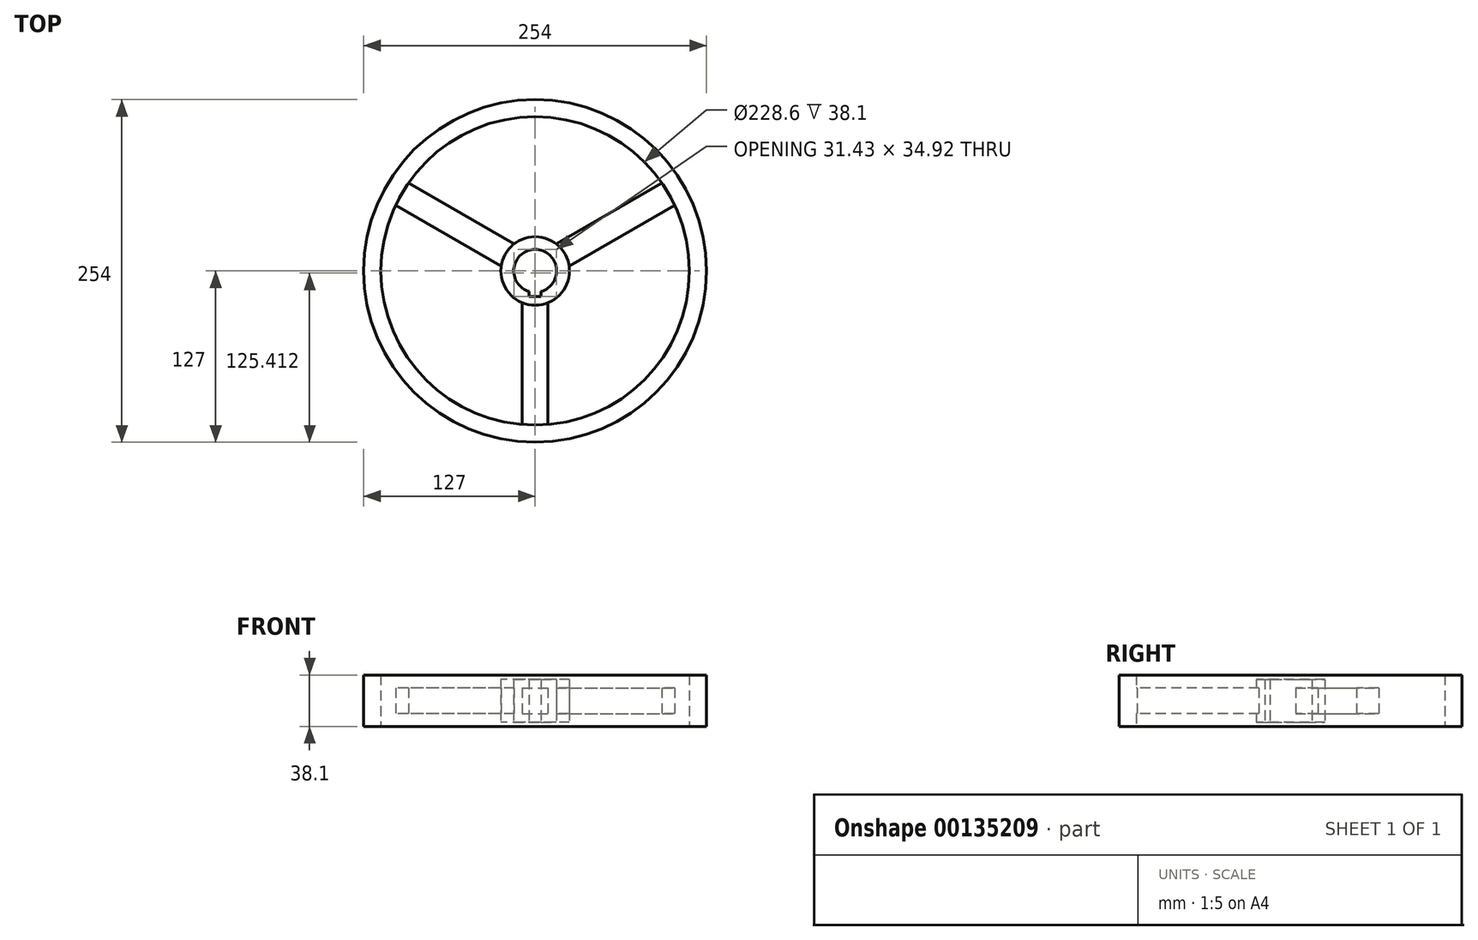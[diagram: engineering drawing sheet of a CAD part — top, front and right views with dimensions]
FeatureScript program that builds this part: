
annotation { "Feature Type Name" : "Feature", "Feature Type Description" : "" }
export const myFeature = defineFeature(function(context is Context, id is Id, definition is map)
    precondition{}
    {
        {
            var Q0;
            Q0=qCreatedBy(makeId("Top.planeOp"),FACE);
            var sketch = newSketch(context, id + "F0", { "sketchPlane" : qUnion([Q0])});
            skLineSegment(sketch, "E0", {"start": v(-303.2, 175.05) * mm, "end": v(0, 0) * mm, "construction": true});
            skLineSegment(sketch, "E1", {"start": v(0, 0) * mm, "end": v(0, -304.21) * mm, "construction": true});
            skArc(sketch, "E2", {"start": v(-98.99, 57.15) * mm, "mid": v(-98.99, -57.15) * mm, "end": v(0, -114.3) * mm});
            skArc(sketch, "E3", {"start": v(-109.99, 63.5) * mm, "mid": v(-109.99, -63.5) * mm, "end": v(0, -127) * mm});
            skArc(sketch, "E4", {"start": v(-13.75, 7.94) * mm, "mid": v(-14.73, -5.91) * mm, "end": v(-4.45, -15.24) * mm});
            skArc(sketch, "E5", {"start": v(-22, 12.7) * mm, "mid": v(-22, -12.7) * mm, "end": v(0, -25.4) * mm});
            skLineSegment(sketch, "E6", {"start": v(-9.53, -23.55) * mm, "end": v(-9.53, -113.9) * mm});
            skLineSegment(sketch, "E7", {"start": v(-25.15, 3.52) * mm, "end": v(-103.4, 48.7) * mm});
            skArc(sketch, "E8", {"start": v(0, -127) * mm, "mid": v(109.99, 63.5) * mm, "end": v(-109.99, 63.5) * mm});
            skArc(sketch, "E9", {"start": v(0, -114.3) * mm, "mid": v(98.99, 57.15) * mm, "end": v(-98.99, 57.15) * mm});
            skArc(sketch, "E10", {"start": v(0, -25.4) * mm, "mid": v(22, 12.7) * mm, "end": v(-22, 12.7) * mm});
            skArc(sketch, "E11", {"start": v(4.44, -15.24) * mm, "mid": v(12.49, 9.8) * mm, "end": v(-13.75, 7.94) * mm});
            skLineSegment(sketch, "E12", {"start": v(9.52, -23.55) * mm, "end": v(9.52, -113.9) * mm});
            skLineSegment(sketch, "E13", {"start": v(-15.63, 20.02) * mm, "end": v(-93.88, 65.2) * mm});
            skLineSegment(sketch, "E14", {"start": v(15.63, 20.02) * mm, "end": v(93.88, 65.2) * mm});
            skLineSegment(sketch, "E15", {"start": v(25.15, 3.52) * mm, "end": v(103.4, 48.7) * mm});
            skLineSegment(sketch, "E16", {"start": v(0, 0) * mm, "end": v(160.47, 92.65) * mm, "construction": true});
            skLineSegment(sketch, "E17", {"start": v(-4.45, -15.24) * mm, "end": v(-4.45, -19.05) * mm});
            skLineSegment(sketch, "E18", {"start": v(-4.45, -19.05) * mm, "end": v(4.44, -19.05) * mm});
            skLineSegment(sketch, "E19", {"start": v(4.44, -19.05) * mm, "end": v(4.44, -15.24) * mm});
            skSolve(sketch);
        }
        {
            var Q0;
            {var subQ5=sQuery(id+"F0.wireOp",EDGE,"E7");Q0=makeQuery(id+"F0.imprint","IMPRINT",FACE,{"disambiguationData":[TD([[makeQuery(id+"F0.imprint","IMPRINT",EDGE,{"derivedFrom":subQ5}),-1.0]])]});}
            var Q1;
            {var subQ5=sQuery(id+"F0.wireOp",EDGE,"E6");Q1=makeQuery(id+"F0.imprint","IMPRINT",FACE,{"disambiguationData":[TD([[makeQuery(id+"F0.imprint","IMPRINT",EDGE,{"derivedFrom":subQ5}),1.0]])]});}
            var Q2;
            {var subQ0=sQuery(id+"F0.wireOp",EDGE,"E14");Q2=makeQuery(id+"F0.imprint","IMPRINT",FACE,{"disambiguationData":[TD([[makeQuery(id+"F0.imprint","IMPRINT",EDGE,{"derivedFrom":subQ0}),-1.0]])]});}
            extrude(context, id + "F1", {"entities" : qUnion([Q0, Q1, Q2]), "endBound" : BoundingType.SYMMETRIC, "depth" : 19.05 * mm});
        }
        {
            var Q0;
            {var subQ7=sQuery(id+"F0.wireOp",EDGE,"E3");Q0=makeQuery(id+"F0.imprint","IMPRINT",FACE,{"disambiguationData":[TD([[makeQuery(id+"F0.imprint","IMPRINT",EDGE,{"derivedFrom":subQ7}),1.0]])]});}
            extrude(context, id + "F2", {"entities" : qUnion([Q0]), "operationType" : NewBodyOperationType.ADD, "endBound" : BoundingType.SYMMETRIC, "depth" : 38.1 * mm});
        }
        {
            var Q0;
            {var subQ4=sQuery(id+"F0.wireOp",EDGE,"E4");Q0=makeQuery(id+"F0.imprint","IMPRINT",FACE,{"disambiguationData":[TD([[makeQuery(id+"F0.imprint","IMPRINT",EDGE,{"derivedFrom":subQ4}),-1.0]])]});}
            extrude(context, id + "F3", {"entities" : qUnion([Q0]), "operationType" : NewBodyOperationType.ADD, "endBound" : BoundingType.SYMMETRIC, "depth" : 31.75 * mm});
        }
    });
